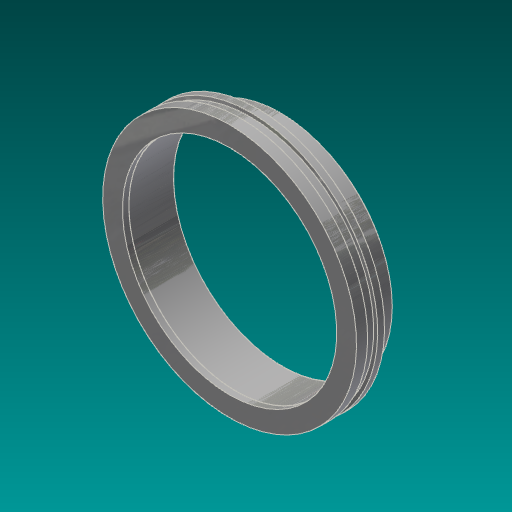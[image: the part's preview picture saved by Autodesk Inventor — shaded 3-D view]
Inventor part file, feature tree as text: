
AUTODESK INVENTOR PART (.ipt)
format: ipt  version: 2017.3 (Build 213256000, 256)  size: 204,800 bytes
history: native  units: in
note: dims shown in document units (in); Inventor stores cm internally (conversion verified against a paired STEP export)
features: revolve x1, chamfer x1, sketch x1
ambient origin geometry x8: Origin, YZ Plane, XZ Plane, XY Plane, X Axis, Y Axis, Z Axis, Center Point
bodies: Solid1 (feature_tree)
feature tree (3):
  revolve  "Revolution1"  [1 undecoded]
  chamfer  "Chamfer2"  Angle=90.0deg  [1 undecoded]
  sketch  "Sketch1"  dims[d0=16.25in d5=1.0in d6=90.0deg d13=18.75in d14=19.25in d16=1.75in d17=1.35in d18=0.0515in d19=0.0842in d20=0.0312in d21=0.125in d22=45.0deg d32=17.0in d33=0.4375in d35=0.0625in d36=0.125in d38=8.0in d43=4.25in d44=0.5in d45=60.0deg d46=0.2577in]
note: 2 required parameter values undecoded (feature->parameter linkage not recoverable at this tier; creation-order binding heuristic only, values carry confidence <= 0.55)